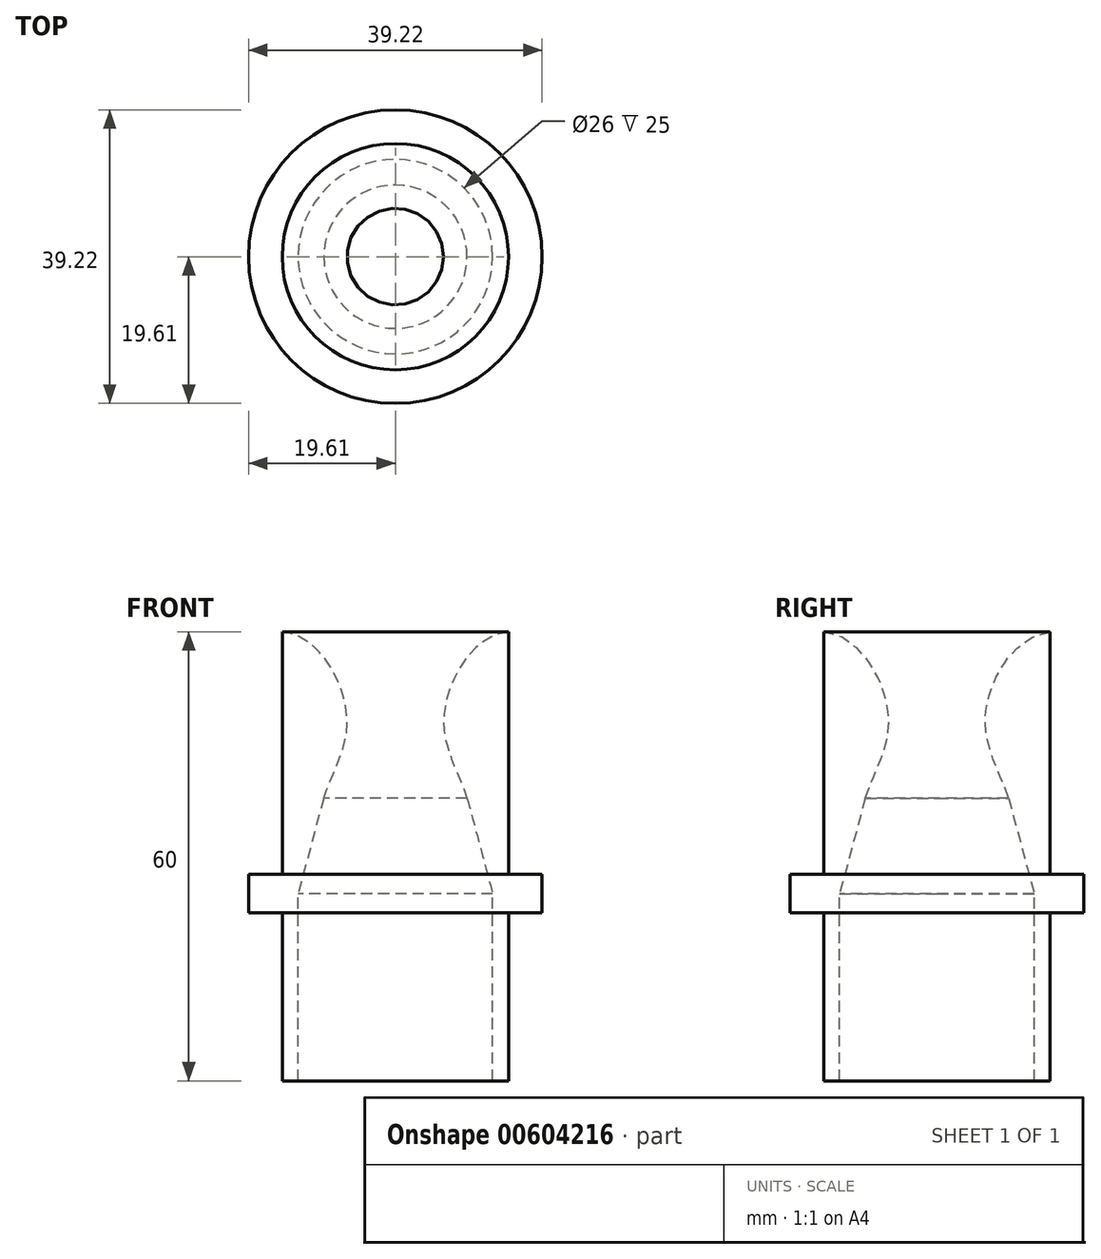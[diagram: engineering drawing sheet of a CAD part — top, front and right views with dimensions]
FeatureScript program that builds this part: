
annotation { "Feature Type Name" : "Feature", "Feature Type Description" : "" }
export const myFeature = defineFeature(function(context is Context, id is Id, definition is map)
    precondition{}
    {
        {
            var Q0;
            Q0=qCreatedBy(makeId("Front.planeOp"),FACE);
            var sketch = newSketch(context, id + "F0", { "sketchPlane" : qUnion([Q0])});
            skLineSegment(sketch, "E0", {"start": v(0, 0) * mm, "end": v(0, -25) * mm, "construction": true});
            skLineSegment(sketch, "E1", {"start": v(0, -25) * mm, "end": v(13, -25) * mm, "construction": true});
            skLineSegment(sketch, "E2", {"start": v(15.12, -25) * mm, "end": v(13, -25) * mm});
            skLineSegment(sketch, "E3", {"start": v(15.12, -25) * mm, "end": v(15.12, 35) * mm});
            skLineSegment(sketch, "E4", {"start": v(19.61, 0) * mm, "end": v(19.61, 2.57) * mm});
            skLineSegment(sketch, "E5", {"start": v(19.61, 2.57) * mm, "end": v(15.12, 2.57) * mm});
            skLineSegment(sketch, "E6", {"start": v(19.61, 0) * mm, "end": v(19.61, -2.57) * mm});
            skLineSegment(sketch, "E7", {"start": v(19.61, -2.57) * mm, "end": v(15.12, -2.57) * mm});
            skLineSegment(sketch, "E8", {"start": v(13, -25) * mm, "end": v(13, 0) * mm});
            skLineSegment(sketch, "E9", {"start": v(13, 0) * mm, "end": v(9.58, 12.78) * mm});
            skFitSpline(sketch, "E10", {"points": [v(15.12, 35) * mm, v(6.5, 23.97) * mm, v(9.58, 12.78) * mm], "startDerivative": vector(-28.88, -3.5) * mm, "endDerivative": vector(9.81, -27.85) * mm});
            skSolve(sketch);
        }
        {
            var Q0;
            {var subQ4=sQuery(id+"F0.wireOp",EDGE,"E2");Q0=makeQuery(id+"F0.imprint","IMPRINT",FACE,{"disambiguationData":[TD([[makeQuery(id+"F0.imprint","IMPRINT",EDGE,{"derivedFrom":subQ4}),-1.0]])]});}
            var Q1;
            Q1=makeQuery(id+"F0.imprint","IMPRINT",FACE,{"disambiguationData":[TD([[makeQuery(id+"F0.imprint","IMPRINT",EDGE,{"derivedFrom":sQuery(id+"F0.wireOp",EDGE,"E4")}),1.0]])]});
            var Q2;
            Q2=sQuery(id+"F0.wireOp",EDGE,"E0");
            revolve(context, id + "F1", {"entities" : qUnion([Q0, Q1]), "axis" : qUnion([Q2]), "revolveType" : RevolveType.FULL});
        }
    });
